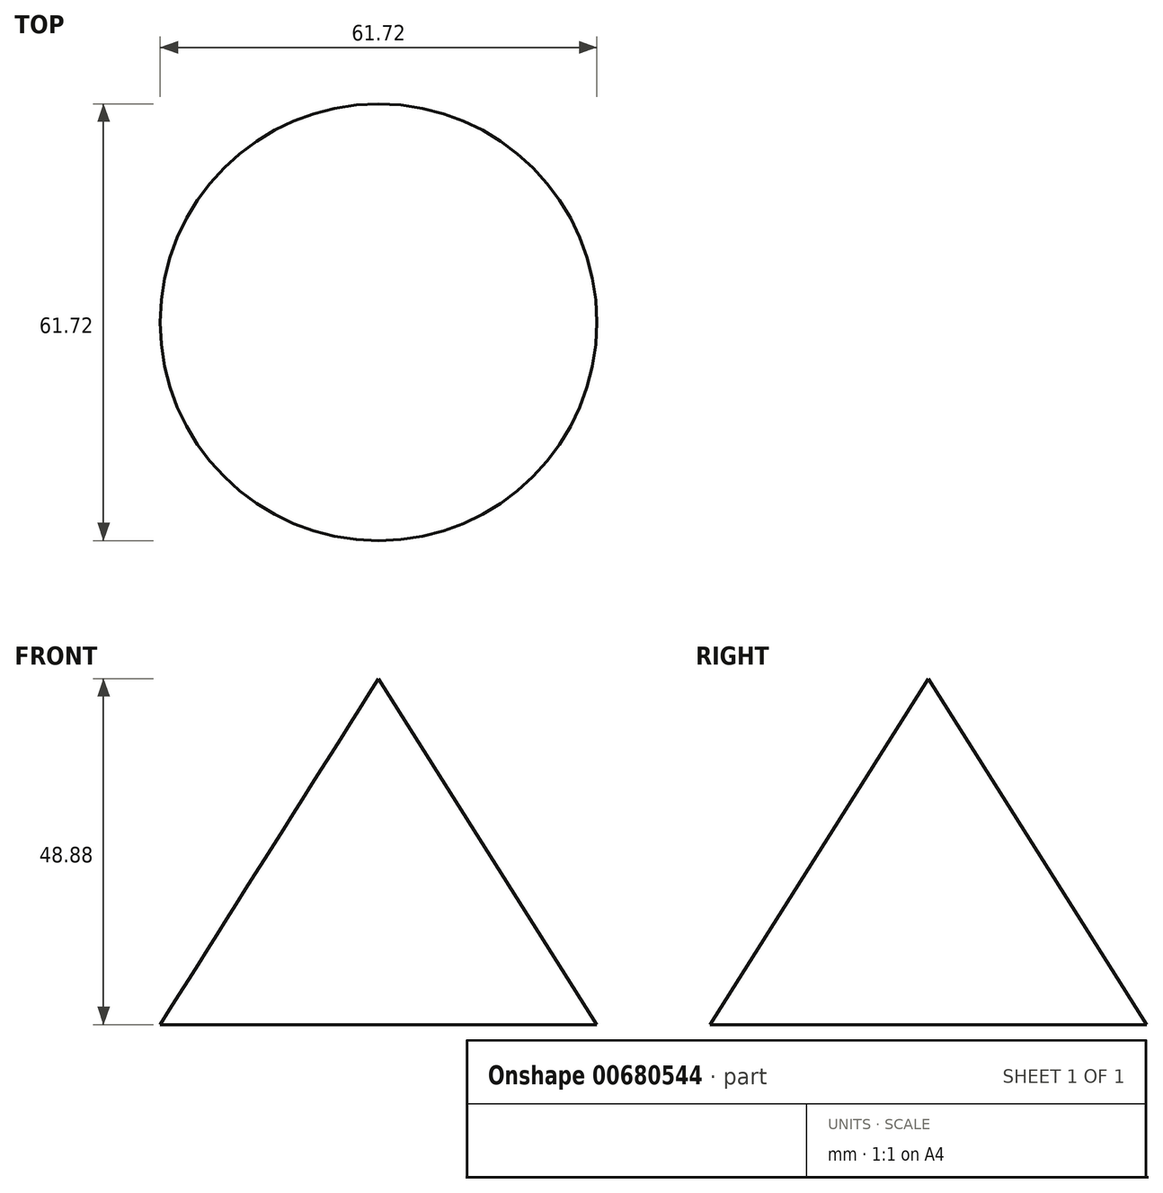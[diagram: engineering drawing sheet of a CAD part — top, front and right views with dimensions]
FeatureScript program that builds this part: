
annotation { "Feature Type Name" : "Feature", "Feature Type Description" : "" }
export const myFeature = defineFeature(function(context is Context, id is Id, definition is map)
    precondition{}
    {
        {
            var Q0;
            Q0=qCreatedBy(makeId("Front.planeOp"),FACE);
            var sketch = newSketch(context, id + "F0", { "sketchPlane" : qUnion([Q0])});
            skLineSegment(sketch, "E0", {"start": v(0, 0) * mm, "end": v(0, 48.88) * mm});
            skLineSegment(sketch, "E1", {"start": v(0, 48.88) * mm, "end": v(30.86, 0) * mm});
            skLineSegment(sketch, "E2", {"start": v(30.86, 0) * mm, "end": v(0, 0) * mm});
            skSolve(sketch);
        }
        {
            var Q0;
            Q0=makeQuery(id+"F0.imprint","IMPRINT",FACE,{"disambiguationData":[TD([[makeQuery(id+"F0.imprint","IMPRINT",EDGE,{"derivedFrom":sQuery(id+"F0.wireOp",EDGE,"E0")}),-1.0]])]});
            var Q1;
            Q1=sQuery(id+"F0.wireOp",EDGE,"E0");
            revolve(context, id + "F1", {"entities" : qUnion([Q0]), "axis" : qUnion([Q1]), "revolveType" : RevolveType.FULL});
        }
    });
